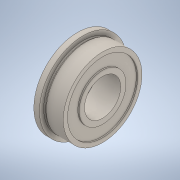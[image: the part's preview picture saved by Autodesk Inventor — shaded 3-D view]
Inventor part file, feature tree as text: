
AUTODESK INVENTOR PART (.ipt)
format: ipt  version: 2020 (Build 240168000, 168)  size: 176,640 bytes
history: native  units: in
note: dims shown in document units (in); Inventor stores cm internally (conversion verified against a paired STEP export)
features: revolve x1
ambient origin geometry x8: Origin, YZ Plane, XZ Plane, XY Plane, X Axis, Y Axis, Z Axis, Center Point
bodies: Solid1 (feature_tree)
feature tree (1):
  revolve  "Revolve1"  [1 undecoded]
note: 1 required parameter value undecoded (feature->parameter linkage not recoverable at this tier; creation-order binding heuristic only, values carry confidence <= 0.55)
